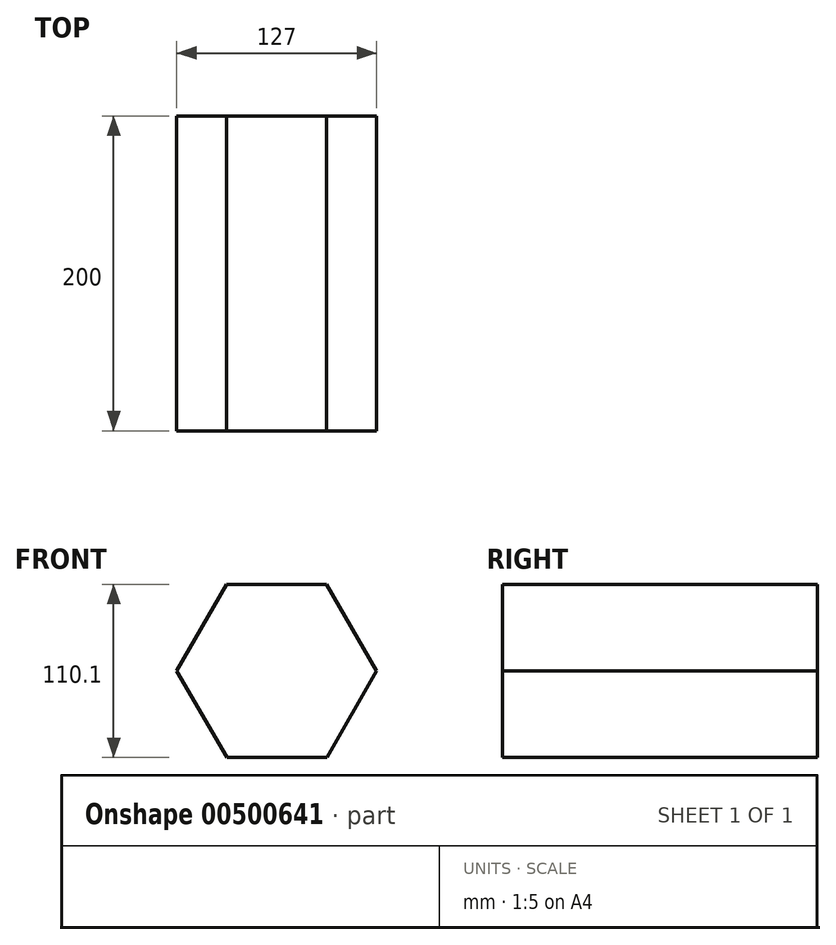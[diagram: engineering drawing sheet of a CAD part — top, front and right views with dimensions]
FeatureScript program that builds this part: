
annotation { "Feature Type Name" : "Feature", "Feature Type Description" : "" }
export const myFeature = defineFeature(function(context is Context, id is Id, definition is map)
    precondition{}
    {
        {
            var Q0;
            Q0=qCreatedBy(makeId("Front.planeOp"),FACE);
            var sketch = newSketch(context, id + "F0", { "sketchPlane" : qUnion([Q0])});
            skCircle(sketch, "E0.cCircle", {"center": v(0, 0) * mm, "radius": 63.5 * mm, "construction": true});
            skLineSegment(sketch, "E0.0", {"start": v(-31.84, 54.94) * mm, "end": v(31.66, 55.05) * mm});
            skLineSegment(sketch, "E0.1", {"start": v(31.66, 55.05) * mm, "end": v(63.5, 0.1) * mm});
            skLineSegment(sketch, "E0.2", {"start": v(63.5, 0.1) * mm, "end": v(31.84, -54.94) * mm});
            skLineSegment(sketch, "E0.3", {"start": v(31.84, -54.94) * mm, "end": v(-31.66, -55.05) * mm});
            skLineSegment(sketch, "E0.4", {"start": v(-31.66, -55.05) * mm, "end": v(-63.5, -0.1) * mm});
            skLineSegment(sketch, "E0.5", {"start": v(-63.5, -0.1) * mm, "end": v(-31.84, 54.94) * mm});
            skSolve(sketch);
        }
        {
            var Q0;
            Q0=makeQuery(id+"F0.imprint","IMPRINT",FACE,{"disambiguationData":[TD([[makeQuery(id+"F0.imprint","IMPRINT",EDGE,{"derivedFrom":sQuery(id+"F0.wireOp",EDGE,"E0.0")}),-1.0]])]});
            extrude(context, id + "F1", {"entities" : qUnion([Q0]), "depth" : 200 * mm});
        }
    });
